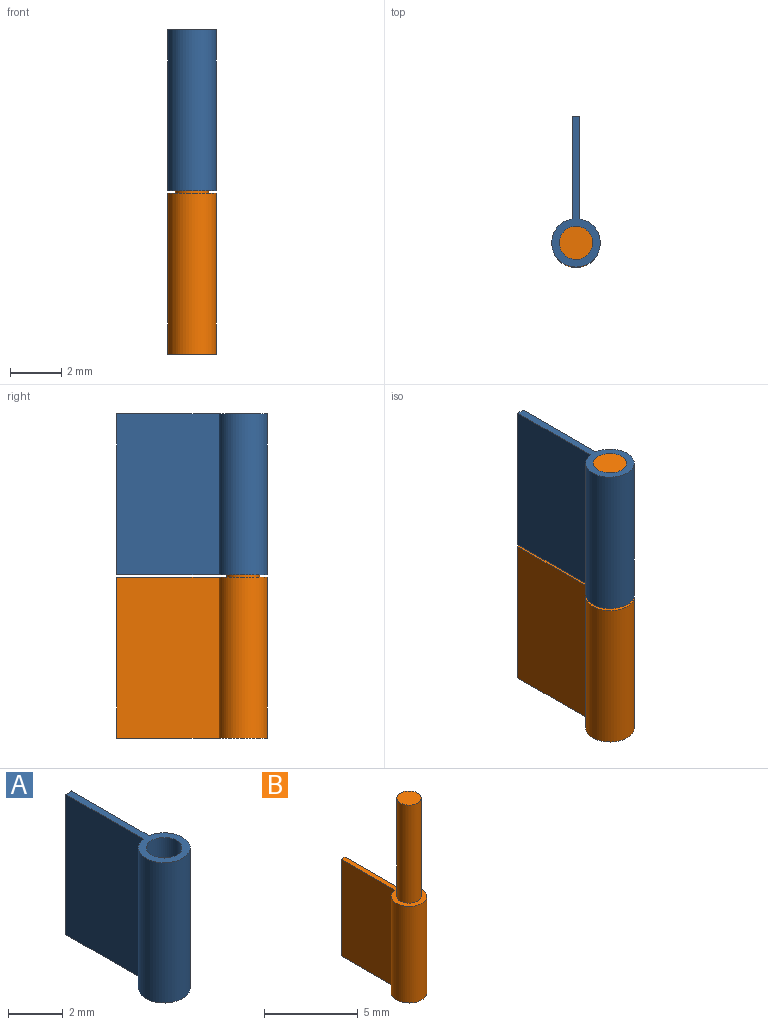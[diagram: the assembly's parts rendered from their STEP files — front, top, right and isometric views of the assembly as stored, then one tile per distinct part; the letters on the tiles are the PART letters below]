
ASSEMBLY  parts=2 mates=1
PART A: 7 faces, bbox 1.9x5.9x6.3 mm
  f0: plane 6.3x4.01mm, normal (1,0,0), area 25.3mm2, adj f1,f4,f5,f6
  f1: plane 6.3x0.3mm, normal (0,1,0), area 1.9mm2, adj f0,f2,f5,f6
  f2: plane 6.3x4.01mm, normal (-1,0,0), area 25.3mm2, adj f1,f4,f5,f6
  f3: cylinder r=0.65mm len=6.3mm, axis (0,0,-1), area 25.7mm2, adj f5,f6
  f4: cylinder r=0.95mm len=6.3mm, axis (0,0,-1), area 35.7mm2, adj f0,f2,f5,f6
  f5: plane 5.9x1.9mm, normal (0,0,1), area 2.7mm2, adj f0,f1,f2,f3,f4
  f6: plane 5.9x1.9mm, normal (0,0,-1), area 2.7mm2, adj f0,f1,f2,f3,f4
PART B: 8 faces, bbox 1.9x5.9x12.7 mm
  f0: plane 6.3x4.01mm, normal (1,0,0), area 25.3mm2, adj f1,f3,f4,f5
  f1: plane 6.3x0.3mm, normal (0,1,0), area 1.9mm2, adj f0,f2,f4,f5
  f2: plane 6.3x4.01mm, normal (-1,0,0), area 25.3mm2, adj f1,f3,f4,f5
  f3: cylinder r=0.95mm len=6.3mm, axis (0,0,-1), area 35.7mm2, adj f0,f2,f4,f5
  f4: plane 5.9x1.9mm, normal (0,0,1), area 2.7mm2, adj f0,f1,f2,f3,f6
  f5: plane 5.9x1.9mm, normal (0,0,-1), area 4mm2, adj f0,f1,f2,f3
  f6: cylinder r=0.65mm len=6.4mm, axis (0,0,-1), area 26.1mm2, adj f4,f7
  f7: plane 1.3x1.3mm, normal (0,0,1), area 1.3mm2, adj f6
PLACE A rot(axis=(0,0,-1),0deg) t=(0,-0.36,0.1)mm
PLACE B t=(0,-0.36,-6.3)mm
MATE revolute A.f3 <-> B.f6  axis (0,0,1) through (0,-1.31,6.4)mm
